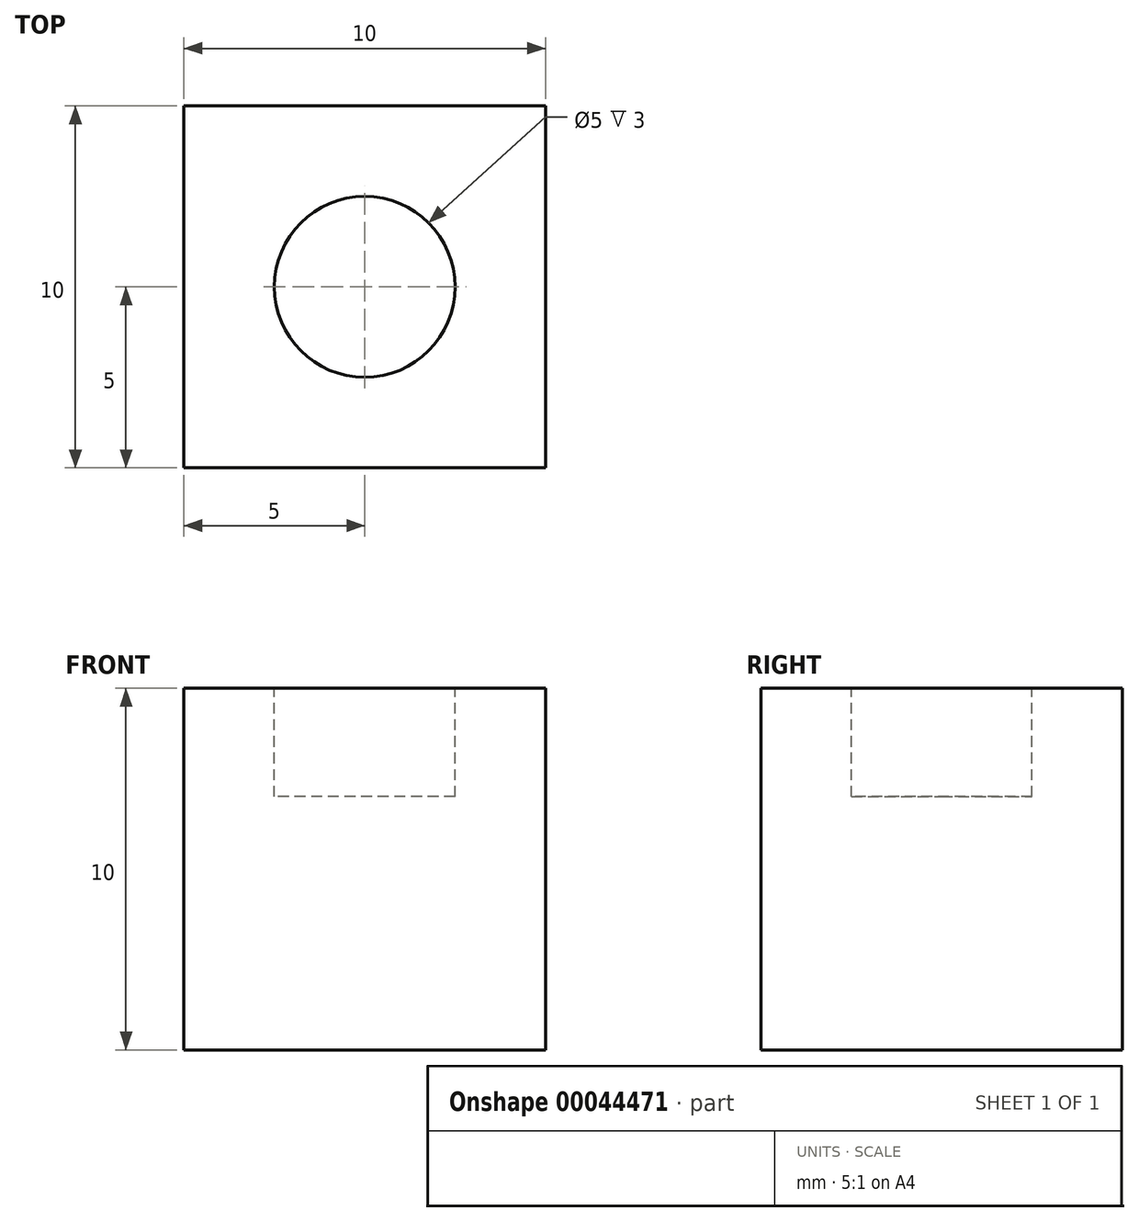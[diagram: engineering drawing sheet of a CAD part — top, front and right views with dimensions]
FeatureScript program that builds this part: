
annotation { "Feature Type Name" : "Feature", "Feature Type Description" : "" }
export const myFeature = defineFeature(function(context is Context, id is Id, definition is map)
    precondition{}
    {
        {
            var Q0;
            Q0=qCreatedBy(makeId("Top.planeOp"),FACE);
            var sketch = newSketch(context, id + "F0", { "sketchPlane" : qUnion([Q0])});
            skLineSegment(sketch, "E0.rect.bottom", {"start": v(5, -5) * mm, "end": v(-5, -5) * mm});
            skLineSegment(sketch, "E0.rect.top", {"start": v(5, 5) * mm, "end": v(-5, 5) * mm});
            skLineSegment(sketch, "E0.rect.left", {"start": v(5, -5) * mm, "end": v(5, 5) * mm});
            skLineSegment(sketch, "E0.rect.right", {"start": v(-5, -5) * mm, "end": v(-5, 5) * mm});
            skPoint(sketch, "E0.rect.middle", {"position": v(0, 0) * mm});
            skSolve(sketch);
        }
        {
            var Q0;
            Q0=makeQuery(id+"F0.imprint","IMPRINT",FACE,{"disambiguationData":[TD([[makeQuery(id+"F0.imprint","IMPRINT",EDGE,{"derivedFrom":sQuery(id+"F0.wireOp",EDGE,"E0.rect.bottom")}),-1.0]])]});
            extrude(context, id + "F1", {"entities" : qUnion([Q0]), "depth" : 10 * mm});
        }
        {
            var Q0;
            Q0=makeQuery(id+"F1.opExtrude","CAP_FACE",FACE,{"disambiguationData":[OSD([sQuery(id+"F0.wireOp",EDGE,"E0.rect.bottom"),sQuery(id+"F0.wireOp",EDGE,"E0.rect.top"),sQuery(id+"F0.wireOp",EDGE,"E0.rect.left"),sQuery(id+"F0.wireOp",EDGE,"E0.rect.right")])],"isStart":false});
            var sketch = newSketch(context, id + "F2", { "sketchPlane" : qUnion([Q0])});
            skCircle(sketch, "E1", {"center": v(0, 0) * mm, "radius": 2.5 * mm});
            skSolve(sketch);
        }
        {
            var Q0;
            Q0 = qSketchRegion(id + "F2", true);
            extrude(context, id + "F3", {"entities" : qUnion([Q0]), "operationType" : NewBodyOperationType.REMOVE, "oppositeDirection" : true, "depth" : 3 * mm});
        }
    });
